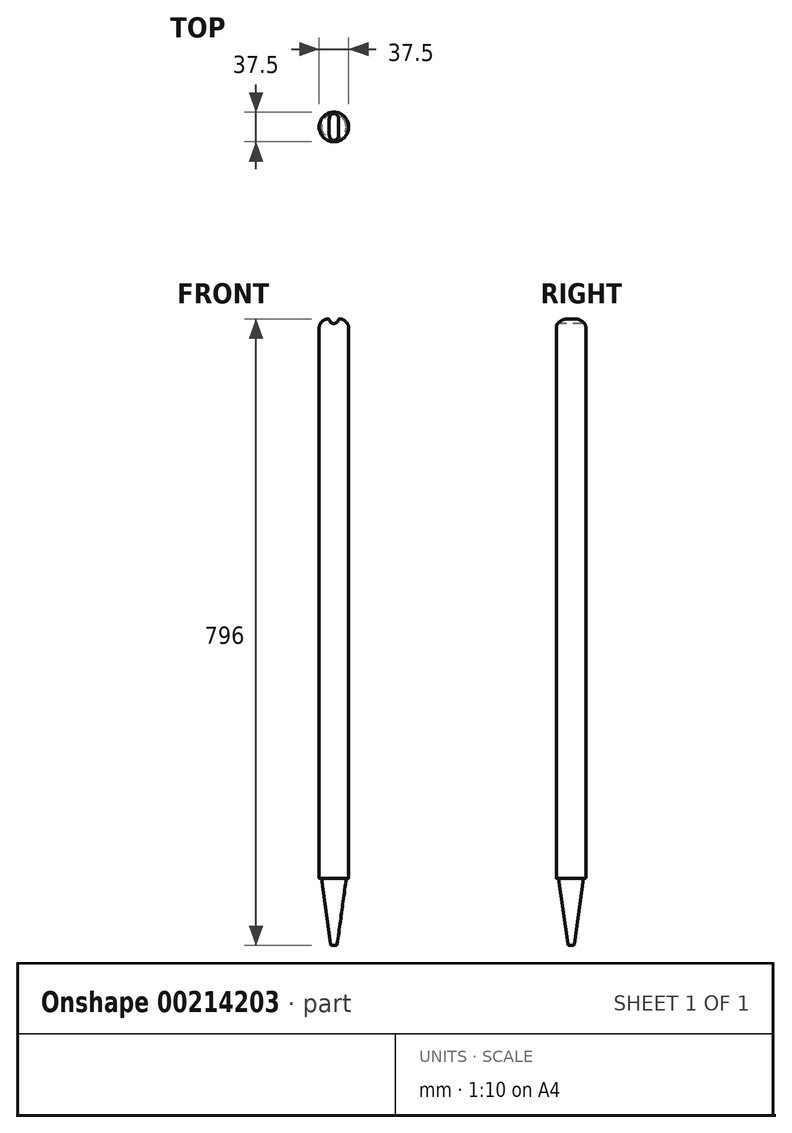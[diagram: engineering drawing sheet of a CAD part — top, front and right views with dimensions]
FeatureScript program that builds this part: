
annotation { "Feature Type Name" : "Feature", "Feature Type Description" : "" }
export const myFeature = defineFeature(function(context is Context, id is Id, definition is map)
    precondition{}
    {
        {
            var Q0;
            Q0=qCreatedBy(makeId("Front.planeOp"),FACE);
            var sketch = newSketch(context, id + "F0", { "sketchPlane" : qUnion([Q0])});
            skLineSegment(sketch, "E0", {"start": v(0, 216.86) * mm, "end": v(0, -155.63) * mm, "construction": true});
            skLineSegment(sketch, "E1", {"start": v(-18.75, 768) * mm, "end": v(-18.75, 86) * mm});
            skLineSegment(sketch, "E2", {"start": v(-17.75, 85) * mm, "end": v(-15.75, 85) * mm});
            skLineSegment(sketch, "E3", {"start": v(-15.75, 85) * mm, "end": v(-4.24, 1.73) * mm});
            skLineSegment(sketch, "E4", {"start": v(-2.26, 0) * mm, "end": v(0, 0) * mm});
            skLineSegment(sketch, "E5", {"start": v(0, 634) * mm, "end": v(0, 0) * mm});
            skPoint(sketch, "E6.visualSharp", {"position": v(-4, 0) * mm});
            skArc(sketch, "E6.filletArc", {"start": v(-4.24, 1.73) * mm, "mid": v(-3.57, 0.5) * mm, "end": v(-2.26, 0) * mm});
            skPoint(sketch, "E7.visualSharp", {"position": v(-18.75, 85) * mm});
            skArc(sketch, "E7.filletArc", {"start": v(-18.75, 86) * mm, "mid": v(-18.46, 85.3) * mm, "end": v(-17.75, 85) * mm});
            skLineSegment(sketch, "E8", {"start": v(-18.75, 768) * mm, "end": v(-18.75, 784) * mm});
            skLineSegment(sketch, "E9", {"start": v(-6.75, 796) * mm, "end": v(0, 796) * mm});
            skLineSegment(sketch, "E10", {"start": v(0, 796) * mm, "end": v(0, 634) * mm});
            skPoint(sketch, "E11.visualSharp", {"position": v(-18.75, 796) * mm});
            skArc(sketch, "E11.filletArc", {"start": v(-6.75, 796) * mm, "mid": v(-15.24, 792.49) * mm, "end": v(-18.75, 784) * mm});
            skSolve(sketch);
        }
        {
            var Q0;
            Q0=makeQuery(id+"F0.imprint","IMPRINT",FACE,{"disambiguationData":[TD([[makeQuery(id+"F0.imprint","IMPRINT",EDGE,{"derivedFrom":sQuery(id+"F0.wireOp",EDGE,"E1")}),1.0]])]});
            var Q1;
            Q1=sQuery(id+"F0.wireOp",EDGE,"E5");
            revolve(context, id + "F1", {"entities" : qUnion([Q0]), "axis" : qUnion([Q1]), "revolveType" : RevolveType.FULL, "surfaceOperationType" : NewSurfaceOperationType.NEW});
        }
        {
            var Q0;
            Q0=qCreatedBy(makeId("Front.planeOp"),FACE);
            var sketch = newSketch(context, id + "F2", { "sketchPlane" : qUnion([Q0])});
            skCircle(sketch, "E12", {"center": v(0, 796) * mm, "radius": 6 * mm});
            skSolve(sketch);
        }
        {
            var Q0;
            Q0 = qSketchRegion(id + "F2", true);
            extrude(context, id + "F3", {"entities" : qUnion([Q0]), "operationType" : NewBodyOperationType.REMOVE, "oppositeDirection" : true, "depth" : 25 * mm, "offsetDistance" : 25 * mm, "hasSecondDirection" : true, "secondDirectionOppositeDirection" : false, "secondDirectionDepth" : 25 * mm});
        }
    });
